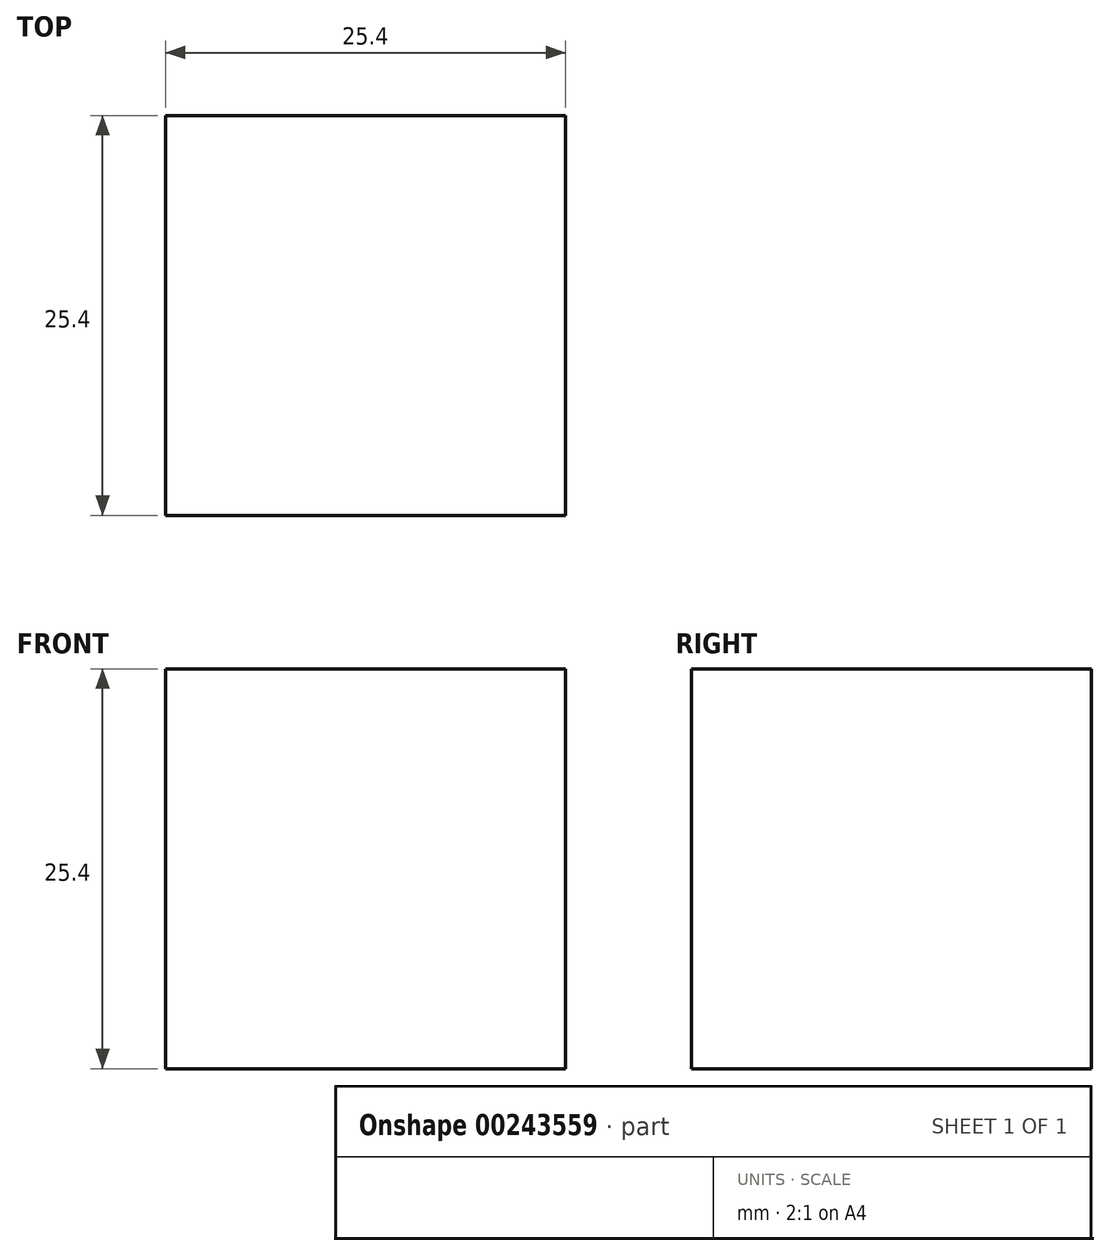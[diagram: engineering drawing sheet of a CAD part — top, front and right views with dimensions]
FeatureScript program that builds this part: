
annotation { "Feature Type Name" : "Feature", "Feature Type Description" : "" }
export const myFeature = defineFeature(function(context is Context, id is Id, definition is map)
    precondition{}
    {
        {
            var Q0;
            Q0=qCreatedBy(makeId("Front.planeOp"),FACE);
            var sketch = newSketch(context, id + "F0", { "sketchPlane" : qUnion([Q0])});
            skLineSegment(sketch, "E0.bottom", {"start": v(-47.12, 25.4) * mm, "end": v(-21.72, 25.4) * mm});
            skLineSegment(sketch, "E0.top", {"start": v(-47.12, 0) * mm, "end": v(-21.72, 0) * mm});
            skLineSegment(sketch, "E0.left", {"start": v(-47.12, 25.4) * mm, "end": v(-47.12, 0) * mm});
            skLineSegment(sketch, "E0.right", {"start": v(-21.72, 25.4) * mm, "end": v(-21.72, 0) * mm});
            skSolve(sketch);
        }
        {
            var Q0;
            Q0 = qSketchRegion(id + "F0", true);
            extrude(context, id + "F1", {"entities" : qUnion([Q0]), "depth" : 25.4 * mm});
        }
    });
